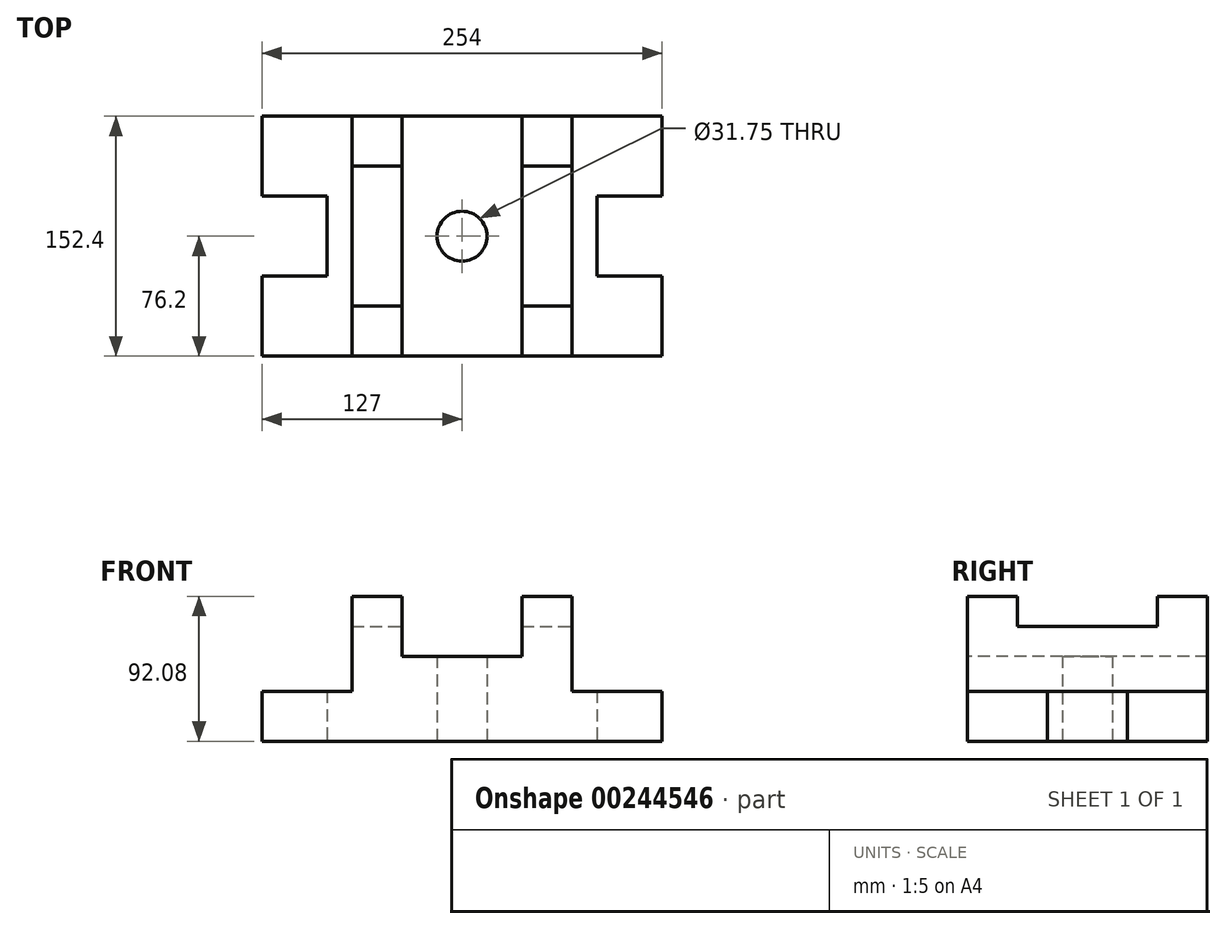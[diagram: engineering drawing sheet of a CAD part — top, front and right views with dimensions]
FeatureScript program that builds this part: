
annotation { "Feature Type Name" : "Feature", "Feature Type Description" : "" }
export const myFeature = defineFeature(function(context is Context, id is Id, definition is map)
    precondition{}
    {
        {
            var Q0;
            Q0=qCreatedBy(makeId("Top.planeOp"),FACE);
            var sketch = newSketch(context, id + "F0", { "sketchPlane" : qUnion([Q0])});
            skLineSegment(sketch, "E0.bottom", {"start": v(127, -76.2) * mm, "end": v(-127, -76.2) * mm});
            skLineSegment(sketch, "E0.top", {"start": v(127, 76.2) * mm, "end": v(-127, 76.2) * mm});
            skLineSegment(sketch, "E0.left", {"start": v(127, -76.2) * mm, "end": v(127, -25.4) * mm});
            skLineSegment(sketch, "E0.right", {"start": v(-127, -76.2) * mm, "end": v(-127, -25.4) * mm});
            skPoint(sketch, "E0.middle", {"position": v(0, 0) * mm});
            skLineSegment(sketch, "E1", {"start": v(127, 25.4) * mm, "end": v(85.72, 25.4) * mm});
            skLineSegment(sketch, "E2", {"start": v(85.72, 25.4) * mm, "end": v(85.72, -25.4) * mm});
            skLineSegment(sketch, "E3", {"start": v(85.72, -25.4) * mm, "end": v(127, -25.4) * mm});
            skLineSegment(sketch, "E4", {"start": v(-127, 25.4) * mm, "end": v(-85.73, 25.4) * mm});
            skLineSegment(sketch, "E5", {"start": v(-85.73, 25.4) * mm, "end": v(-85.73, -25.4) * mm});
            skLineSegment(sketch, "E6", {"start": v(-85.73, -25.4) * mm, "end": v(-127, -25.4) * mm});
            skLineSegment(sketch, "E7.trimOffspring", {"start": v(-127, 25.4) * mm, "end": v(-127, 76.2) * mm});
            skLineSegment(sketch, "E8.trimOffspring", {"start": v(127, 25.4) * mm, "end": v(127, 76.2) * mm});
            skLineSegment(sketch, "E9", {"start": v(-38.1, 76.2) * mm, "end": v(-38.1, -76.2) * mm});
            skLineSegment(sketch, "E10", {"start": v(38.1, 76.2) * mm, "end": v(38.1, -76.2) * mm});
            skLineSegment(sketch, "E11", {"start": v(-69.85, 76.2) * mm, "end": v(-69.85, -76.2) * mm});
            skLineSegment(sketch, "E12", {"start": v(69.85, 76.2) * mm, "end": v(69.85, -76.2) * mm});
            skLineSegment(sketch, "E13", {"start": v(-69.85, 44.45) * mm, "end": v(-38.1, 44.45) * mm});
            skLineSegment(sketch, "E14", {"start": v(-69.85, -44.45) * mm, "end": v(-38.1, -44.45) * mm});
            skLineSegment(sketch, "E15", {"start": v(38.1, 44.45) * mm, "end": v(69.85, 44.45) * mm});
            skLineSegment(sketch, "E16", {"start": v(38.1, -44.45) * mm, "end": v(69.85, -44.45) * mm});
            skCircle(sketch, "E17", {"center": v(0, 0) * mm, "radius": 15.88 * mm});
            skSolve(sketch);
        }
        {
            var Q0;
            Q0 = qSketchRegion(id + "F0", true);
            extrude(context, id + "F1", {"entities" : qUnion([Q0]), "depth" : 31.75 * mm});
        }
        {
            var Q0;
            Q0=makeQuery(id+"F0.imprint","IMPRINT",FACE,{"disambiguationData":[TD([[makeQuery(id+"F0.imprint","IMPRINT",EDGE,{"derivedFrom":sQuery(id+"F0.wireOp",EDGE,"E17")}),-1.0]])]});
            extrude(context, id + "F2", {"entities" : qUnion([Q0]), "operationType" : NewBodyOperationType.ADD, "depth" : 53.97 * mm});
        }
        {
            var Q0;
            {var subQ5=sQuery(id+"F0.wireOp",EDGE,"E13");Q0=makeQuery(id+"F0.imprint","IMPRINT",FACE,{"disambiguationData":[TD([[makeQuery(id+"F0.imprint","IMPRINT",EDGE,{"derivedFrom":subQ5}),1.0]])]});}
            var Q1;
            {var subQ5=sQuery(id+"F0.wireOp",EDGE,"E14");Q1=makeQuery(id+"F0.imprint","IMPRINT",FACE,{"disambiguationData":[TD([[makeQuery(id+"F0.imprint","IMPRINT",EDGE,{"derivedFrom":subQ5}),-1.0]])]});}
            var Q2;
            {var subQ5=sQuery(id+"F0.wireOp",EDGE,"E16");Q2=makeQuery(id+"F0.imprint","IMPRINT",FACE,{"disambiguationData":[TD([[makeQuery(id+"F0.imprint","IMPRINT",EDGE,{"derivedFrom":subQ5}),-1.0]])]});}
            var Q3;
            {var subQ5=sQuery(id+"F0.wireOp",EDGE,"E15");Q3=makeQuery(id+"F0.imprint","IMPRINT",FACE,{"disambiguationData":[TD([[makeQuery(id+"F0.imprint","IMPRINT",EDGE,{"derivedFrom":subQ5}),1.0]])]});}
            extrude(context, id + "F3", {"entities" : qUnion([Q0, Q1, Q2, Q3]), "operationType" : NewBodyOperationType.ADD, "depth" : 92.07 * mm});
        }
        {
            var Q0;
            {var subQ0=sQuery(id+"F0.wireOp",EDGE,"E13");Q0=makeQuery(id+"F0.imprint","IMPRINT",FACE,{"disambiguationData":[TD([[makeQuery(id+"F0.imprint","IMPRINT",EDGE,{"derivedFrom":subQ0}),-1.0]])]});}
            var Q1;
            {var subQ0=sQuery(id+"F0.wireOp",EDGE,"E15");Q1=makeQuery(id+"F0.imprint","IMPRINT",FACE,{"disambiguationData":[TD([[makeQuery(id+"F0.imprint","IMPRINT",EDGE,{"derivedFrom":subQ0}),-1.0]])]});}
            extrude(context, id + "F4", {"entities" : qUnion([Q0, Q1]), "operationType" : NewBodyOperationType.ADD, "depth" : 73.02 * mm});
        }
    });
